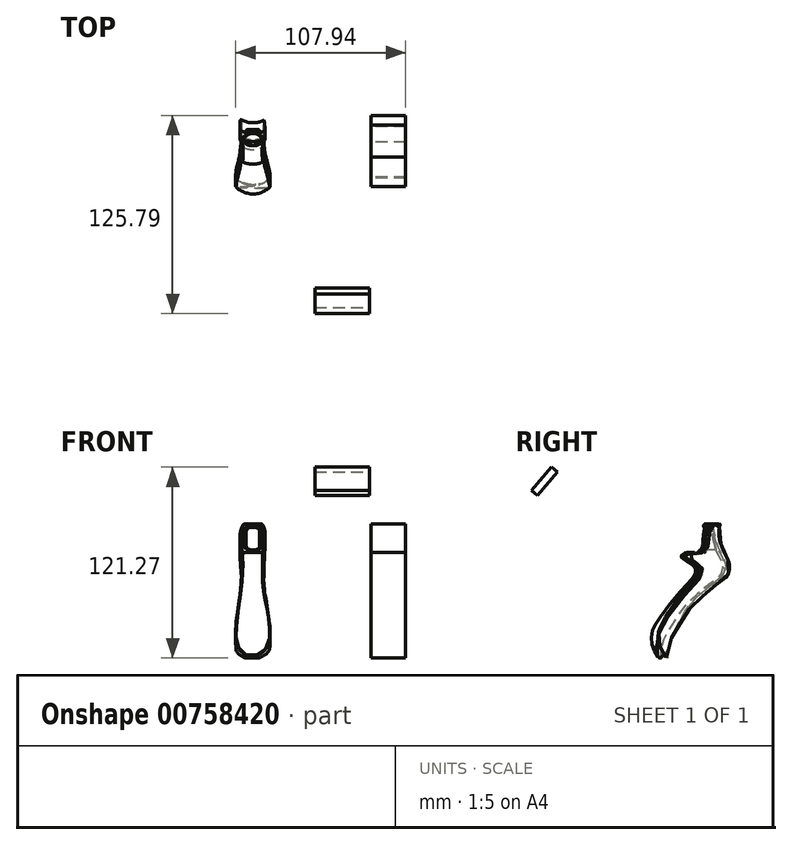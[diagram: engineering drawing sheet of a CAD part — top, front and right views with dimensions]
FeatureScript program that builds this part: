
annotation { "Feature Type Name" : "Feature", "Feature Type Description" : "" }
export const myFeature = defineFeature(function(context is Context, id is Id, definition is map)
    precondition{}
    {
        {
            var Q0;
            Q0=qCreatedBy(makeId("Right.planeOp"),FACE);
            var sketch = newSketch(context, id + "F0", { "sketchPlane" : qUnion([Q0])});
            skFitSpline(sketch, "E0", {"points": [v(68.93, -10.81) * mm, v(66.67, -7.42) * mm, v(65.05, -4.2) * mm, v(64.4, 0) * mm, v(64.4, 4.36) * mm, v(66.67, 9.7) * mm, v(76.03, 22.77) * mm, v(86.52, 35.2) * mm, v(91.36, 40.36) * mm, v(92.5, 43.1) * mm, v(91.53, 46.66) * mm, v(88.14, 49.4) * mm, v(84.1, 51.98) * mm, v(83.2, 52.8) * mm, v(83.55, 53.95) * mm, v(85.95, 55.37) * mm, v(88.29, 55.89) * mm, v(92.1, 55.55) * mm, v(93.42, 55.77) * mm, v(94.8, 56.86) * mm, v(95.88, 60.34) * mm, v(96.39, 66.9) * mm, v(97.3, 71.7) * mm, v(97.93, 73.52) * mm, v(99.59, 73.75) * mm, v(102.33, 73.75) * mm, v(103.47, 73.7) * mm, v(103, 72.32) * mm, v(102.55, 66.9) * mm, v(104.78, 58.28) * mm, v(108.15, 51.5) * mm, v(109.4, 47.27) * mm, v(108.43, 41.85) * mm, v(103.7, 37.34) * mm, v(98.04, 33.12) * mm, v(92.28, 28.15) * mm, v(86, 22.1) * mm, v(81.27, 15.94) * mm, v(76.99, 9.09) * mm, v(73.5, 3.38) * mm, v(71.22, -2.55) * mm, v(69.9, -8.83) * mm, v(69.88, -10.36) * mm, v(70.32, -11.25) * mm, v(69.68, -11.23) * mm, v(68.93, -10.81) * mm]});
            skSolve(sketch);
        }
        {
            var Q0;
            Q0=qCreatedBy(makeId("Top.planeOp"),FACE);
            cPlane(context, id + "F1", {"entities" : qUnion([Q0]), "cplaneType" : CPlaneType.OFFSET, "offset" : 13.3 * mm, "oppositeDirection" : true, "width" : 150 * mm, "height" : 150 * mm});
        }
        {
            var Q0;
            Q0=qCreatedBy(makeId("Front.planeOp"),FACE);
            var sketch = newSketch(context, id + "F2", { "sketchPlane" : qUnion([Q0])});
            skLineSegment(sketch, "E1.bottom", {"start": v(-75.54, 62.8) * mm, "end": v(-43.91, 62.8) * mm});
            skLineSegment(sketch, "E1.top", {"start": v(-75.54, 28.7) * mm, "end": v(-43.91, 28.7) * mm});
            skLineSegment(sketch, "E1.left", {"start": v(-75.54, 62.8) * mm, "end": v(-75.54, 28.7) * mm});
            skLineSegment(sketch, "E1.right", {"start": v(-43.91, 62.8) * mm, "end": v(-43.91, 28.7) * mm});
            skSolve(sketch);
        }
        {
            var Q0;
            Q0=makeQuery(id+"F2.imprint","IMPRINT",FACE,{"disambiguationData":[TD([[makeQuery(id+"F2.imprint","IMPRINT",EDGE,{"derivedFrom":sQuery(id+"F2.wireOp",EDGE,"E1.bottom")}),-1.0]])]});
            extrude(context, id + "F3", {"entities" : qUnion([Q0]), "depth" : 5 * mm, "offsetDistance" : 25 * mm});
        }
        {
            var Q0;
            Q0=makeQuery(id+"F3.opExtrude","SWEPT_BODY",BODY,{"disambiguationData":[OSD([sQuery(id+"F2.wireOp",EDGE,"E1.bottom"),sQuery(id+"F2.wireOp",EDGE,"E1.top"),sQuery(id+"F2.wireOp",EDGE,"E1.left"),sQuery(id+"F2.wireOp",EDGE,"E1.right")])]});
            var Q1;
            Q1=makeQuery(id+"F3.opExtrude","CAP_EDGE",EDGE,{"disambiguationData":[OSD([sQuery(id+"F2.wireOp",EDGE,"E1.bottom")])],"isStart":true});
            transform(context, id + "F4", {"entities" : qUnion([Q0]), "transformType" : TransformType.ROTATION, "transformAxis" : qUnion([Q1]), "angle" : 15 * degree, "oppositeDirection" : true, "makeCopy" : false});
        }
        {
            var Q0;
            Q0=makeQuery(id+"F3.opExtrude","SWEPT_BODY",BODY,{"disambiguationData":[OSD([sQuery(id+"F2.wireOp",EDGE,"E1.bottom"),sQuery(id+"F2.wireOp",EDGE,"E1.top"),sQuery(id+"F2.wireOp",EDGE,"E1.left"),sQuery(id+"F2.wireOp",EDGE,"E1.right")])]});
            transform(context, id + "F5", {"entities" : qUnion([Q0]), "transformType" : TransformType.TRANSLATION_3D, "dx" : -200.4 * mm, "dy" : 0 * mm, "dz" : 0 * mm, "makeCopy" : false});
        }
        {
            var Q0;
            Q0=makeQuery(id+"F3.opExtrude","SWEPT_BODY",BODY,{"disambiguationData":[OSD([sQuery(id+"F2.wireOp",EDGE,"E1.bottom"),sQuery(id+"F2.wireOp",EDGE,"E1.top"),sQuery(id+"F2.wireOp",EDGE,"E1.left"),sQuery(id+"F2.wireOp",EDGE,"E1.right")])]});
            var Q1;
            Q1=makeQuery(id+"Flpr5LHeYpND3I0_4.opExtrude","SWEPT_BODY",BODY,{"disambiguationData":[OSD([sQuery(id+"FyDyzudHODPkHYP_4.wireOp",EDGE,"m75Vnbgv-jhCc-RTIO-U7NT-55jqRwHsRLKe.bottom"),sQuery(id+"FyDyzudHODPkHYP_4.wireOp",EDGE,"m75Vnbgv-jhCc-RTIO-U7NT-55jqRwHsRLKe.top"),sQuery(id+"FyDyzudHODPkHYP_4.wireOp",EDGE,"m75Vnbgv-jhCc-RTIO-U7NT-55jqRwHsRLKe.left"),sQuery(id+"FyDyzudHODPkHYP_4.wireOp",EDGE,"m75Vnbgv-jhCc-RTIO-U7NT-55jqRwHsRLKe.right")])]});
            deleteBodies(context, id + "F6", {"entities" : qUnion([Q0, Q1])});
        }
        {
            var Q0;
            Q0=makeQuery(id+"F0.imprint","IMPRINT",FACE,{"disambiguationData":[TD([[makeQuery(id+"F0.imprint","IMPRINT",EDGE,{"derivedFrom":sQuery(id+"F0.wireOp",EDGE,"E0")}),-1.0]])]});
            extrude(context, id + "F7", {"entities" : qUnion([Q0]), "depth" : 22 * mm, "offsetDistance" : 25 * mm});
        }
        {
            var Q0;
            Q0=makeQuery(id+"F7.opExtrude","SWEPT_BODY",BODY,{"disambiguationData":[OSD([sQuery(id+"F0.wireOp",EDGE,"E0")])]});
            transform(context, id + "F8", {"entities" : qUnion([Q0]), "transformType" : TransformType.TRANSLATION_3D, "dx" : -100 * mm, "dy" : 0 * mm, "dz" : 0 * mm, "makeCopy" : false});
        }
        {
            var Q0;
            Q0=makeQuery(id+"F7.opExtrude","CAP_FACE",FACE,{"disambiguationData":[OSD([sQuery(id+"F0.wireOp",EDGE,"E0")])],"isStart":true});
            extrude(context, id + "F9", {"entities" : qUnion([Q0]), "depth" : 25 * mm, "offsetDistance" : 25 * mm});
        }
        {
            var Q0;
            Q0=makeQuery(id+"F9.opExtrude","SWEPT_BODY",BODY,{"disambiguationData":[OSD([sQuery(id+"F0.wireOp",EDGE,"E0")])]});
            transform(context, id + "F10", {"entities" : qUnion([Q0]), "transformType" : TransformType.TRANSLATION_3D, "dx" : -64 * mm, "dy" : 0 * mm, "dz" : 0 * mm, "makeCopy" : false});
        }
        {
            var Q0;
            Q0=makeQuery(id+"F9.opExtrude","CAP_FACE",FACE,{"disambiguationData":[OSD([sQuery(id+"F0.wireOp",EDGE,"E0")])],"isStart":false});
            extrude(context, id + "F11", {"entities" : qUnion([Q0]), "operationType" : NewBodyOperationType.REMOVE, "oppositeDirection" : true, "depth" : 24.5 * mm, "offsetDistance" : 25 * mm});
        }
        {
            var Q0;
            Q0=qCreatedBy(id+"F1.planeOp",FACE);
            var sketch = newSketch(context, id + "F12", { "sketchPlane" : qUnion([Q0])});
            skArc(sketch, "E2", {"start": v(-186.3, 70.25) * mm, "mid": v(-175.3, 65.62) * mm, "end": v(-164.3, 70.25) * mm});
            skSolve(sketch);
        }
        {
            var Q0;
            Q0=makeQuery(id+"F9.opExtrude","CAP_FACE",FACE,{"disambiguationData":[OSD([sQuery(id+"F0.wireOp",EDGE,"E0")])],"isStart":true});
            var Q1;
            Q1=sQuery(id+"F12.wireOp",EDGE,"E2");
            sweep(context, id + "F13", {"operationType" : NewBodyOperationType.ADD, "profiles" : qUnion([Q0]), "path" : qUnion([Q1]), "keepProfileOrientation" : true});
        }
        {
            var Q0;
            Q0=qCreatedBy(makeId("Front.planeOp"),FACE);
            var sketch = newSketch(context, id + "F14", { "sketchPlane" : qUnion([Q0])});
            skLineSegment(sketch, "E3.bottom", {"start": v(-135.67, 106.74) * mm, "end": v(-100.86, 106.74) * mm});
            skLineSegment(sketch, "E3.top", {"start": v(-135.67, 87.28) * mm, "end": v(-100.86, 87.28) * mm});
            skLineSegment(sketch, "E3.left", {"start": v(-135.67, 106.74) * mm, "end": v(-135.67, 87.28) * mm});
            skLineSegment(sketch, "E3.right", {"start": v(-100.86, 106.74) * mm, "end": v(-100.86, 87.28) * mm});
            skSolve(sketch);
        }
        {
            var Q0;
            Q0=makeQuery(id+"F14.imprint","IMPRINT",FACE,{"disambiguationData":[TD([[makeQuery(id+"F14.imprint","IMPRINT",EDGE,{"derivedFrom":sQuery(id+"F14.wireOp",EDGE,"E3.bottom")}),-1.0]])]});
            extrude(context, id + "F15", {"entities" : qUnion([Q0]), "depth" : 5 * mm, "offsetDistance" : 25 * mm});
        }
        {
            var Q0;
            Q0=makeQuery(id+"F15.opExtrude","SWEPT_BODY",BODY,{"disambiguationData":[OSD([sQuery(id+"F14.wireOp",EDGE,"E3.bottom"),sQuery(id+"F14.wireOp",EDGE,"E3.top"),sQuery(id+"F14.wireOp",EDGE,"E3.left"),sQuery(id+"F14.wireOp",EDGE,"E3.right")])]});
            var Q1;
            Q1=makeQuery(id+"F15.opExtrude","CAP_EDGE",EDGE,{"disambiguationData":[OSD([sQuery(id+"F14.wireOp",EDGE,"E3.bottom")])],"isStart":true});
            transform(context, id + "F16", {"entities" : qUnion([Q0]), "transformType" : TransformType.ROTATION, "transformAxis" : qUnion([Q1]), "angle" : 40 * degree, "oppositeDirection" : true, "makeCopy" : false});
        }
        {
            var Q0;
            Q0=makeQuery(id+"F15.opExtrude","CAP_FACE",FACE,{"disambiguationData":[OSD([sQuery(id+"F14.wireOp",EDGE,"E3.bottom"),sQuery(id+"F14.wireOp",EDGE,"E3.top"),sQuery(id+"F14.wireOp",EDGE,"E3.left"),sQuery(id+"F14.wireOp",EDGE,"E3.right")])],"isStart":true});
            cPlane(context, id + "F17", {"entities" : qUnion([Q0]), "cplaneType" : CPlaneType.OFFSET, "offset" : 98.7 * mm, "width" : 150 * mm, "height" : 150 * mm});
        }
        {
            var Q0;
            Q0=qCreatedBy(id+"F17.planeOp",FACE);
            cPlane(context, id + "F18", {"entities" : qUnion([Q0]), "cplaneType" : CPlaneType.OFFSET, "offset" : 10 * mm, "oppositeDirection" : true, "width" : 150 * mm, "height" : 150 * mm});
        }
        {
            var Q0;
            Q0=qCreatedBy(id+"F18.planeOp",FACE);
            var sketch = newSketch(context, id + "F19", { "sketchPlane" : qUnion([Q0])});
            skFitSpline(sketch, "E4", {"points": [v(175.64, 33.07) * mm, v(172.83, 33.51) * mm, v(168.55, 35.15) * mm, v(165.26, 38.72) * mm, v(164.18, 42.88) * mm, v(164.22, 48.05) * mm, v(164.86, 55.18) * mm, v(166.02, 64.8) * mm, v(167.3, 73.6) * mm, v(168.03, 81.77) * mm, v(168.43, 89.02) * mm, v(168.1, 97.51) * mm, v(167.87, 105.96) * mm, v(167.46, 114.17) * mm, v(169.55, 118.1) * mm, v(172.7, 119.63) * mm, v(177.76, 119.42) * mm, v(181.36, 117.22) * mm, v(183.16, 112.21) * mm, v(182.64, 102.96) * mm, v(182.2, 94.43) * mm, v(182.52, 84.06) * mm, v(183.53, 71.28) * mm, v(184.69, 61.59) * mm, v(185.4, 55.54) * mm, v(185.8, 50.5) * mm, v(185.93, 44) * mm, v(185.09, 38.52) * mm, v(182.4, 35.47) * mm, v(179.12, 33.75) * mm, v(175.64, 33.07) * mm]});
            skSolve(sketch);
        }
        {
            var Q0;
            Q0=makeQuery(id+"F19.imprint","IMPRINT",FACE,{"disambiguationData":[TD([[makeQuery(id+"F19.imprint","IMPRINT",EDGE,{"derivedFrom":sQuery(id+"F19.wireOp",EDGE,"E4")}),-1.0]])]});
            extrude(context, id + "F20", {"entities" : qUnion([Q0]), "depth" : 50 * mm, "offsetDistance" : 25 * mm});
        }
        {
            var Q0;
            Q0=makeQuery(id+"F20.opExtrude","SWEPT_BODY",BODY,{"disambiguationData":[OSD([sQuery(id+"F19.wireOp",EDGE,"E4")])]});
            var Q1;
            Q1=makeQuery(id+"F9.opExtrude","SWEPT_BODY",BODY,{"disambiguationData":[OSD([sQuery(id+"F0.wireOp",EDGE,"E0")])]});
            var Q2;
            Q2=makeQuery(id+"F9.opExtrude","SWEPT_BODY",BODY,{"disambiguationData":[OSD([sQuery(id+"F0.wireOp",EDGE,"E0")])]});
            booleanBodies(context, id + "F21", {"operationType" : BooleanOperationType.INTERSECTION, "tools" : qUnion([Q0, Q1]), "targets" : qUnion([Q2])});
        }
        {
            var Q0;
            Q0=qCreatedBy(makeId("Front.planeOp"),FACE);
            cPlane(context, id + "F22", {"entities" : qUnion([Q0]), "cplaneType" : CPlaneType.OFFSET, "offset" : 61 * mm, "oppositeDirection" : true, "width" : 150 * mm, "height" : 150 * mm});
        }
        {
            var Q0;
            Q0=qCreatedBy(id+"F22.planeOp",FACE);
            var sketch = newSketch(context, id + "F23", { "sketchPlane" : qUnion([Q0])});
            skLineSegment(sketch, "E5.bottom", {"start": v(-176.34, 71.61) * mm, "end": v(-173.68, 71.61) * mm});
            skLineSegment(sketch, "E5.top", {"start": v(-176.34, 57.43) * mm, "end": v(-173.68, 57.43) * mm});
            skLineSegment(sketch, "E5.left", {"start": v(-179.34, 68.61) * mm, "end": v(-179.34, 60.43) * mm});
            skLineSegment(sketch, "E5.right", {"start": v(-170.68, 68.61) * mm, "end": v(-170.68, 60.43) * mm});
            skPoint(sketch, "E6.visualSharp", {"position": v(-179.34, 71.61) * mm});
            skArc(sketch, "E6.filletArc", {"start": v(-176.34, 71.61) * mm, "mid": v(-178.46, 70.73) * mm, "end": v(-179.34, 68.61) * mm});
            skPoint(sketch, "E7.visualSharp", {"position": v(-170.68, 71.61) * mm});
            skArc(sketch, "E7.filletArc", {"start": v(-170.68, 68.61) * mm, "mid": v(-171.56, 70.73) * mm, "end": v(-173.68, 71.61) * mm});
            skPoint(sketch, "E8.visualSharp", {"position": v(-179.34, 57.43) * mm});
            skArc(sketch, "E8.filletArc", {"start": v(-179.34, 60.43) * mm, "mid": v(-178.46, 58.31) * mm, "end": v(-176.34, 57.43) * mm});
            skPoint(sketch, "E9.visualSharp", {"position": v(-170.68, 57.43) * mm});
            skArc(sketch, "E9.filletArc", {"start": v(-173.68, 57.43) * mm, "mid": v(-171.56, 58.31) * mm, "end": v(-170.68, 60.43) * mm});
            skSolve(sketch);
        }
        {
            var Q0;
            Q0=makeQuery(id+"F23.imprint","IMPRINT",FACE,{"disambiguationData":[TD([[makeQuery(id+"F23.imprint","IMPRINT",EDGE,{"derivedFrom":sQuery(id+"F23.wireOp",EDGE,"E5.bottom")}),-1.0]])]});
            extrude(context, id + "F24", {"entities" : qUnion([Q0]), "operationType" : NewBodyOperationType.REMOVE, "oppositeDirection" : true, "depth" : 100 * mm, "offsetDistance" : 25 * mm});
        }
        {
            var Q0;
            Q0=makeQuery(id+"F21.opBoolean","SPLIT",FACE,{"disambiguationData":[TD([makeQuery(id+"F20.opExtrude","SWEPT_FACE",FACE,{"disambiguationData":[OSD([sQuery(id+"F19.wireOp",EDGE,"E4")])]})])],"derivedFrom":makeQuery(id+"F13.opSweep","SWEPT_FACE",FACE,{"disambiguationData":[OSD([sQuery(id+"F0.wireOp",EDGE,"E0"),sQuery(id+"F12.wireOp",EDGE,"E2")])]})});
            fillet(context, id + "F25", {"entities" : qUnion([Q0]), "radius" : 1 * mm, "tangentPropagation" : true, "allowEdgeOverflow" : false});
        }
    });
